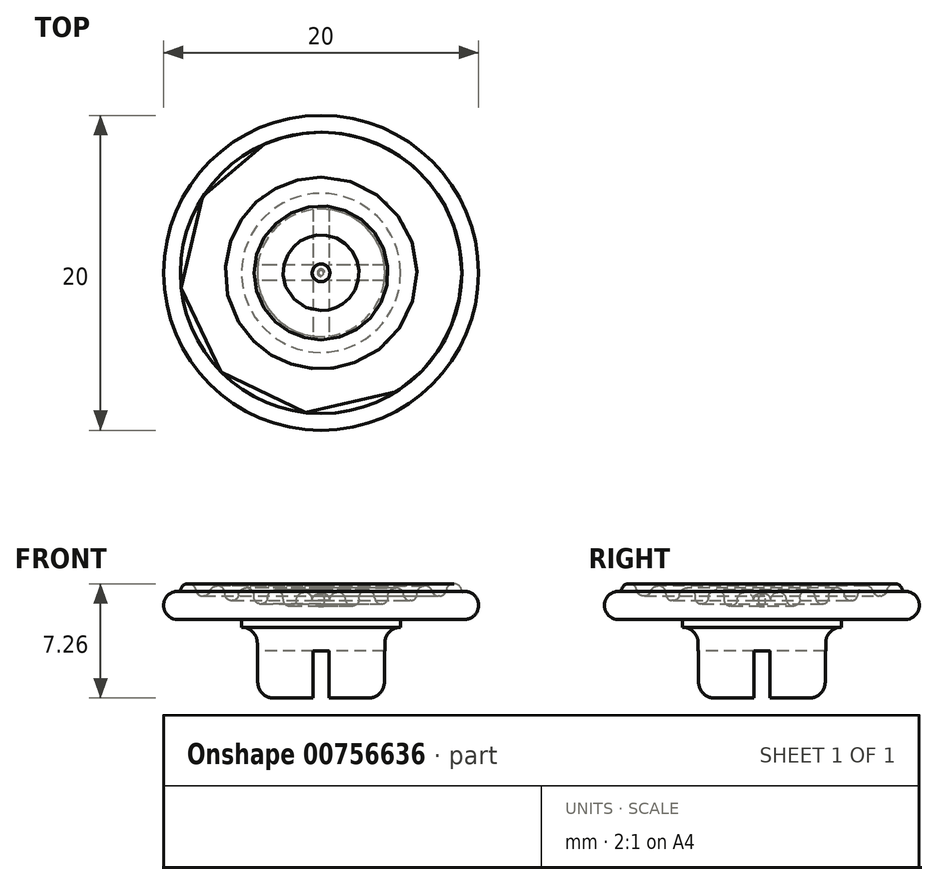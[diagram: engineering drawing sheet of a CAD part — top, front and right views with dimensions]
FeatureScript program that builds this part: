
annotation { "Feature Type Name" : "Feature", "Feature Type Description" : "" }
export const myFeature = defineFeature(function(context is Context, id is Id, definition is map)
    precondition{}
    {
        {
            var Q0;
            Q0=qCreatedBy(makeId("Right.planeOp"),FACE);
            var sketch = newSketch(context, id + "F0", { "sketchPlane" : qUnion([Q0])});
            skLineSegment(sketch, "E0.bottom", {"start": v(0, 4.5) * mm, "end": v(4.05, 4.5) * mm});
            skLineSegment(sketch, "E0.top", {"start": v(0, 0) * mm, "end": v(4.05, 0) * mm});
            skLineSegment(sketch, "E0.left", {"start": v(0, 4.5) * mm, "end": v(0, 0) * mm});
            skLineSegment(sketch, "E0.right", {"start": v(4.05, 4.5) * mm, "end": v(4.05, 0) * mm});
            skLineSegment(sketch, "E1.bottom", {"start": v(0, 5) * mm, "end": v(4, 5) * mm});
            skLineSegment(sketch, "E1.left", {"start": v(0, 5) * mm, "end": v(0, 4.5) * mm});
            skLineSegment(sketch, "E2.bottom", {"start": v(0, 7) * mm, "end": v(10, 7) * mm});
            skLineSegment(sketch, "E2.top", {"start": v(0, 5) * mm, "end": v(10, 5) * mm});
            skLineSegment(sketch, "E2.left", {"start": v(0, 7) * mm, "end": v(0, 5) * mm});
            skLineSegment(sketch, "E2.right", {"start": v(10, 7) * mm, "end": v(10, 5) * mm});
            skCircle(sketch, "E3", {"center": v(0, 48.4) * mm, "radius": 42.6 * mm});
            skLineSegment(sketch, "E4.bottom", {"start": v(0, 5) * mm, "end": v(5.05, 5) * mm});
            skLineSegment(sketch, "E4.top", {"start": v(0, 4.5) * mm, "end": v(5.05, 4.5) * mm});
            skLineSegment(sketch, "E4.right", {"start": v(5.05, 5) * mm, "end": v(5.05, 4.5) * mm});
            skSolve(sketch);
        }
        {
            var Q0;
            Q0=makeQuery(id+"F0.imprint","IMPRINT",FACE,{"disambiguationData":[TD([[makeQuery(id+"F0.imprint","IMPRINT",EDGE,{"derivedFrom":sQuery(id+"F0.wireOp",EDGE,"E0.bottom")}),1.0]])]});
            var Q1;
            {var subQ1=sQuery(id+"F0.wireOp",EDGE,"E1.bottom");Q1=makeQuery(id+"F0.imprint","IMPRINT",FACE,{"disambiguationData":[TD([[makeQuery(id+"F0.imprint","IMPRINT",EDGE,{"derivedFrom":subQ1}),1.0]])]});}
            var Q2;
            Q2=makeQuery(id+"F0.imprint","IMPRINT",FACE,{"disambiguationData":[TD([[makeQuery(id+"F0.imprint","IMPRINT",EDGE,{"derivedFrom":sQuery(id+"F0.wireOp",EDGE,"E0.bottom")}),-1.0]])]});
            var Q3;
            Q3=sQuery(id+"F0.wireOp",EDGE,"E0.left");
            revolve(context, id + "F1", {"surfaceOperationType" : NewSurfaceOperationType.NEW, "entities" : qUnion([Q0, Q1, Q2]), "axis" : qUnion([Q3]), "revolveType" : RevolveType.FULL});
        }
        {
            var Q0;
            Q0=makeQuery(id+"F1.opRevolve","SWEPT_FACE",FACE,{"disambiguationData":[OSD([sQuery(id+"F0.wireOp",EDGE,"E2.right")])]});
            fillet(context, id + "F2", {"entities" : qUnion([Q0]), "radius" : 0.88 * mm, "tangentPropagation" : true, "allowEdgeOverflow" : false});
        }
        {
            var Q0;
            Q0=qCreatedBy(makeId("Front.planeOp"),FACE);
            var sketch = newSketch(context, id + "F3", { "sketchPlane" : qUnion([Q0])});
            skCircle(sketch, "E5", {"center": v(1.06, 6.23) * mm, "radius": 0.5 * mm});
            skLineSegment(sketch, "E6", {"start": v(0, 10.44) * mm, "end": v(0, -4.27) * mm});
            skCircle(sketch, "E7.1.0.0", {"center": v(2.9, 6.36) * mm, "radius": 0.5 * mm});
            skCircle(sketch, "E7.2.0.0", {"center": v(4.75, 6.5) * mm, "radius": 0.5 * mm});
            skCircle(sketch, "E7.3.0.0", {"center": v(6.6, 6.63) * mm, "radius": 0.5 * mm});
            skCircle(sketch, "E7.4.0.0", {"center": v(8.44, 6.76) * mm, "radius": 0.5 * mm});
            skLineSegment(sketch, "E7.direction1", {"start": v(1.06, 6.23) * mm, "end": v(2.9, 6.36) * mm, "construction": true});
            skSolve(sketch);
        }
        {
            var Q0;
            Q0 = qSketchRegion(id + "F3", true);
            var Q1;
            Q1=makeQuery(id+"F0.imprint","IMPRINT",FACE,{"disambiguationData":[TD([[makeQuery(id+"F0.imprint","IMPRINT",EDGE,{"derivedFrom":sQuery(id+"F0.wireOp",EDGE,"E0.bottom")}),1.0]])]});
            var Q2;
            Q2=sQuery(id+"F3.wireOp",EDGE,"E6");
            revolve(context, id + "F4", {"surfaceOperationType" : NewSurfaceOperationType.NEW, "entities" : qUnion([Q0, Q1]), "axis" : qUnion([Q2]), "revolveType" : RevolveType.FULL});
        }
        {
            var Q0;
            Q0=makeQuery(id+"F4.opRevolve","SWEPT_BODY",BODY,{"disambiguationData":[OSD([sQuery(id+"F3.wireOp",EDGE,"E5")])]});
            var Q1;
            Q1=makeQuery(id+"F4.opRevolve","SWEPT_BODY",BODY,{"disambiguationData":[OSD([sQuery(id+"F3.wireOp",EDGE,"E7.4.0.0")])]});
            var Q2;
            Q2=makeQuery(id+"F4.opRevolve","SWEPT_BODY",BODY,{"disambiguationData":[OSD([sQuery(id+"F3.wireOp",EDGE,"E7.3.0.0")])]});
            var Q3;
            Q3=makeQuery(id+"F4.opRevolve","SWEPT_BODY",BODY,{"disambiguationData":[OSD([sQuery(id+"F3.wireOp",EDGE,"E7.2.0.0")])]});
            var Q4;
            Q4=makeQuery(id+"F1.opRevolve","SWEPT_BODY",BODY,{"disambiguationData":[OSD([sQuery(id+"F0.wireOp",EDGE,"E0.top"),sQuery(id+"F0.wireOp",EDGE,"E0.left"),sQuery(id+"F0.wireOp",EDGE,"E0.right"),sQuery(id+"F0.wireOp",EDGE,"E1.left"),sQuery(id+"F0.wireOp",EDGE,"E2.top"),sQuery(id+"F0.wireOp",EDGE,"E2.left"),sQuery(id+"F0.wireOp",EDGE,"E2.right"),sQuery(id+"F0.wireOp",EDGE,"E3"),sQuery(id+"F0.wireOp",EDGE,"E4.top"),sQuery(id+"F0.wireOp",EDGE,"E4.right")])]});
            var Q5;
            Q5=makeQuery(id+"F4.opRevolve","SWEPT_BODY",BODY,{"disambiguationData":[OSD([sQuery(id+"F3.wireOp",EDGE,"E7.1.0.0")])]});
            var Q6;
            Q6=makeQuery(id+"F4.opRevolve","SWEPT_BODY",BODY,{"disambiguationData":[OSD([sQuery(id+"F0.wireOp",EDGE,"E0.bottom"),sQuery(id+"F0.wireOp",EDGE,"E1.bottom"),sQuery(id+"F0.wireOp",EDGE,"E1.left"),sQuery(id+"F0.wireOp",EDGE,"E2.top"),sQuery(id+"F0.wireOp",EDGE,"E4.top"),sQuery(id+"F0.wireOp",EDGE,"E4.right")])]});
            var Q7;
            Q7=makeQuery(id+"F1.opRevolve","SWEPT_BODY",BODY,{"disambiguationData":[OSD([sQuery(id+"F0.wireOp",EDGE,"E0.top"),sQuery(id+"F0.wireOp",EDGE,"E0.left"),sQuery(id+"F0.wireOp",EDGE,"E0.right"),sQuery(id+"F0.wireOp",EDGE,"E1.left"),sQuery(id+"F0.wireOp",EDGE,"E2.top"),sQuery(id+"F0.wireOp",EDGE,"E2.left"),sQuery(id+"F0.wireOp",EDGE,"E2.right"),sQuery(id+"F0.wireOp",EDGE,"E3"),sQuery(id+"F0.wireOp",EDGE,"E4.top"),sQuery(id+"F0.wireOp",EDGE,"E4.right")])]});
            booleanBodies(context, id + "F5", {"operationType" : BooleanOperationType.UNION, "tools" : qUnion([Q0, Q1, Q2, Q3, Q4, Q5, Q6, Q7])});
        }
        {
            var Q0;
            Q0=makeQuery(id+"F5.opBoolean","INTERSECT",EDGE,{"derivedFrom":[makeQuery(id+"F1.opRevolve","SWEPT_FACE",FACE,{"disambiguationData":[OSD([sQuery(id+"F0.wireOp",EDGE,"E3")])]}),makeQuery(id+"F4.opRevolve","SWEPT_FACE",FACE,{"disambiguationData":[OSD([sQuery(id+"F3.wireOp",EDGE,"E7.4.0.0")])]})]});
            var Q1;
            Q1=makeQuery(id+"F5.opBoolean","INTERSECT",EDGE,{"derivedFrom":[makeQuery(id+"F1.opRevolve","SWEPT_FACE",FACE,{"disambiguationData":[OSD([sQuery(id+"F0.wireOp",EDGE,"E3")])]}),makeQuery(id+"F4.opRevolve","SWEPT_FACE",FACE,{"disambiguationData":[OSD([sQuery(id+"F3.wireOp",EDGE,"E7.4.0.0")])]})]});
            var Q2;
            Q2=makeQuery(id+"F5.opBoolean","INTERSECT",EDGE,{"disambiguationData":[OD(1.0)],"derivedFrom":[makeQuery(id+"F1.opRevolve","SWEPT_FACE",FACE,{"disambiguationData":[OSD([sQuery(id+"F0.wireOp",EDGE,"E3")])]}),makeQuery(id+"F4.opRevolve","SWEPT_FACE",FACE,{"disambiguationData":[OSD([sQuery(id+"F3.wireOp",EDGE,"E7.3.0.0")])]})]});
            var Q3;
            Q3=makeQuery(id+"F4.opRevolve","SWEPT_FACE",FACE,{"disambiguationData":[OSD([sQuery(id+"F3.wireOp",EDGE,"E7.3.0.0")])]});
            var Q4;
            Q4=makeQuery(id+"F5.opBoolean","INTERSECT",EDGE,{"disambiguationData":[OD(1.0)],"derivedFrom":[makeQuery(id+"F1.opRevolve","SWEPT_FACE",FACE,{"disambiguationData":[OSD([sQuery(id+"F0.wireOp",EDGE,"E3")])]}),makeQuery(id+"F4.opRevolve","SWEPT_FACE",FACE,{"disambiguationData":[OSD([sQuery(id+"F3.wireOp",EDGE,"E7.2.0.0")])]})]});
            var Q5;
            Q5=makeQuery(id+"F5.opBoolean","INTERSECT",EDGE,{"disambiguationData":[OD(0.0)],"derivedFrom":[makeQuery(id+"F1.opRevolve","SWEPT_FACE",FACE,{"disambiguationData":[OSD([sQuery(id+"F0.wireOp",EDGE,"E3")])]}),makeQuery(id+"F4.opRevolve","SWEPT_FACE",FACE,{"disambiguationData":[OSD([sQuery(id+"F3.wireOp",EDGE,"E7.2.0.0")])]})]});
            var Q6;
            Q6=makeQuery(id+"F5.opBoolean","INTERSECT",EDGE,{"disambiguationData":[OD(1.0)],"derivedFrom":[makeQuery(id+"F1.opRevolve","SWEPT_FACE",FACE,{"disambiguationData":[OSD([sQuery(id+"F0.wireOp",EDGE,"E3")])]}),makeQuery(id+"F4.opRevolve","SWEPT_FACE",FACE,{"disambiguationData":[OSD([sQuery(id+"F3.wireOp",EDGE,"E7.1.0.0")])]})]});
            var Q7;
            Q7=makeQuery(id+"F5.opBoolean","INTERSECT",EDGE,{"disambiguationData":[OD(0.0)],"derivedFrom":[makeQuery(id+"F1.opRevolve","SWEPT_FACE",FACE,{"disambiguationData":[OSD([sQuery(id+"F0.wireOp",EDGE,"E3")])]}),makeQuery(id+"F4.opRevolve","SWEPT_FACE",FACE,{"disambiguationData":[OSD([sQuery(id+"F3.wireOp",EDGE,"E7.1.0.0")])]})]});
            var Q8;
            Q8=makeQuery(id+"F5.opBoolean","INTERSECT",EDGE,{"disambiguationData":[OD(1.0)],"derivedFrom":[makeQuery(id+"F1.opRevolve","SWEPT_FACE",FACE,{"disambiguationData":[OSD([sQuery(id+"F0.wireOp",EDGE,"E3")])]}),makeQuery(id+"F4.opRevolve","SWEPT_FACE",FACE,{"disambiguationData":[OSD([sQuery(id+"F3.wireOp",EDGE,"E5")])]})]});
            var Q9;
            Q9=makeQuery(id+"F5.opBoolean","INTERSECT",EDGE,{"disambiguationData":[OD(0.0)],"derivedFrom":[makeQuery(id+"F1.opRevolve","SWEPT_FACE",FACE,{"disambiguationData":[OSD([sQuery(id+"F0.wireOp",EDGE,"E3")])]}),makeQuery(id+"F4.opRevolve","SWEPT_FACE",FACE,{"disambiguationData":[OSD([sQuery(id+"F3.wireOp",EDGE,"E5")])]})]});
            fillet(context, id + "F6", {"entities" : qUnion([Q0, Q1, Q2, Q3, Q4, Q5, Q6, Q7, Q8, Q9]), "radius" : 0.4 * mm, "tangentPropagation" : true, "allowEdgeOverflow" : false});
        }
        {
            var Q0;
            Q0=makeQuery(id+"F1.opRevolve","SWEPT_EDGE",EDGE,{"disambiguationData":[OSD([sQuery(id+"F0.wireOp",EDGE,"E0.bottom"),sQuery(id+"F0.wireOp",EDGE,"E0.right"),sQuery(id+"F0.wireOp",EDGE,"E4.top")])]});
            var Q1;
            Q1=makeQuery(id+"F1.opRevolve","SWEPT_EDGE",EDGE,{"disambiguationData":[OSD([sQuery(id+"F0.wireOp",EDGE,"E0.top"),sQuery(id+"F0.wireOp",EDGE,"E0.right")])]});
            fillet(context, id + "F7", {"entities" : qUnion([Q0, Q1]), "radius" : 1 * mm, "tangentPropagation" : true, "allowEdgeOverflow" : false});
        }
        {
            var Q0;
            Q0=qCreatedBy(makeId("Top.planeOp"),FACE);
            var sketch = newSketch(context, id + "F8", { "sketchPlane" : qUnion([Q0])});
            skLineSegment(sketch, "E8.bottom", {"start": v(0.5, 15) * mm, "end": v(-0.5, 15) * mm});
            skLineSegment(sketch, "E8.top", {"start": v(0.5, -15) * mm, "end": v(-0.5, -15) * mm});
            skLineSegment(sketch, "E8.left", {"start": v(0.5, 15) * mm, "end": v(0.5, 0.5) * mm});
            skLineSegment(sketch, "E8.right", {"start": v(-0.5, 15) * mm, "end": v(-0.5, 0.5) * mm});
            skPoint(sketch, "E8.middle", {"position": v(0, 0) * mm});
            skLineSegment(sketch, "E9.bottom", {"start": v(15, -0.5) * mm, "end": v(0.5, -0.5) * mm});
            skLineSegment(sketch, "E9.top", {"start": v(15, 0.5) * mm, "end": v(0.5, 0.5) * mm});
            skLineSegment(sketch, "E9.left", {"start": v(15, -0.5) * mm, "end": v(15, 0.5) * mm});
            skLineSegment(sketch, "E9.right", {"start": v(-15, -0.5) * mm, "end": v(-15, 0.5) * mm});
            skLineSegment(sketch, "E10.trimOffspring", {"start": v(-0.5, -0.5) * mm, "end": v(-0.5, -15) * mm});
            skLineSegment(sketch, "E11.trimOffspring", {"start": v(-0.5, 0.5) * mm, "end": v(-15, 0.5) * mm});
            skLineSegment(sketch, "E12.trimOffspring", {"start": v(0.5, -0.5) * mm, "end": v(0.5, -15) * mm});
            skLineSegment(sketch, "E13.trimOffspring", {"start": v(-0.5, -0.5) * mm, "end": v(-15, -0.5) * mm});
            skSolve(sketch);
        }
        {
            var Q0;
            Q0=makeQuery(id+"F8.imprint","IMPRINT",FACE,{"disambiguationData":[TD([[makeQuery(id+"F8.imprint","IMPRINT",EDGE,{"derivedFrom":sQuery(id+"F8.wireOp",EDGE,"E8.bottom")}),1.0]])]});
            extrude(context, id + "F9", {"entities" : qUnion([Q0]), "operationType" : NewBodyOperationType.REMOVE, "depth" : 3 * mm, "offsetDistance" : 25 * mm});
        }
    });
